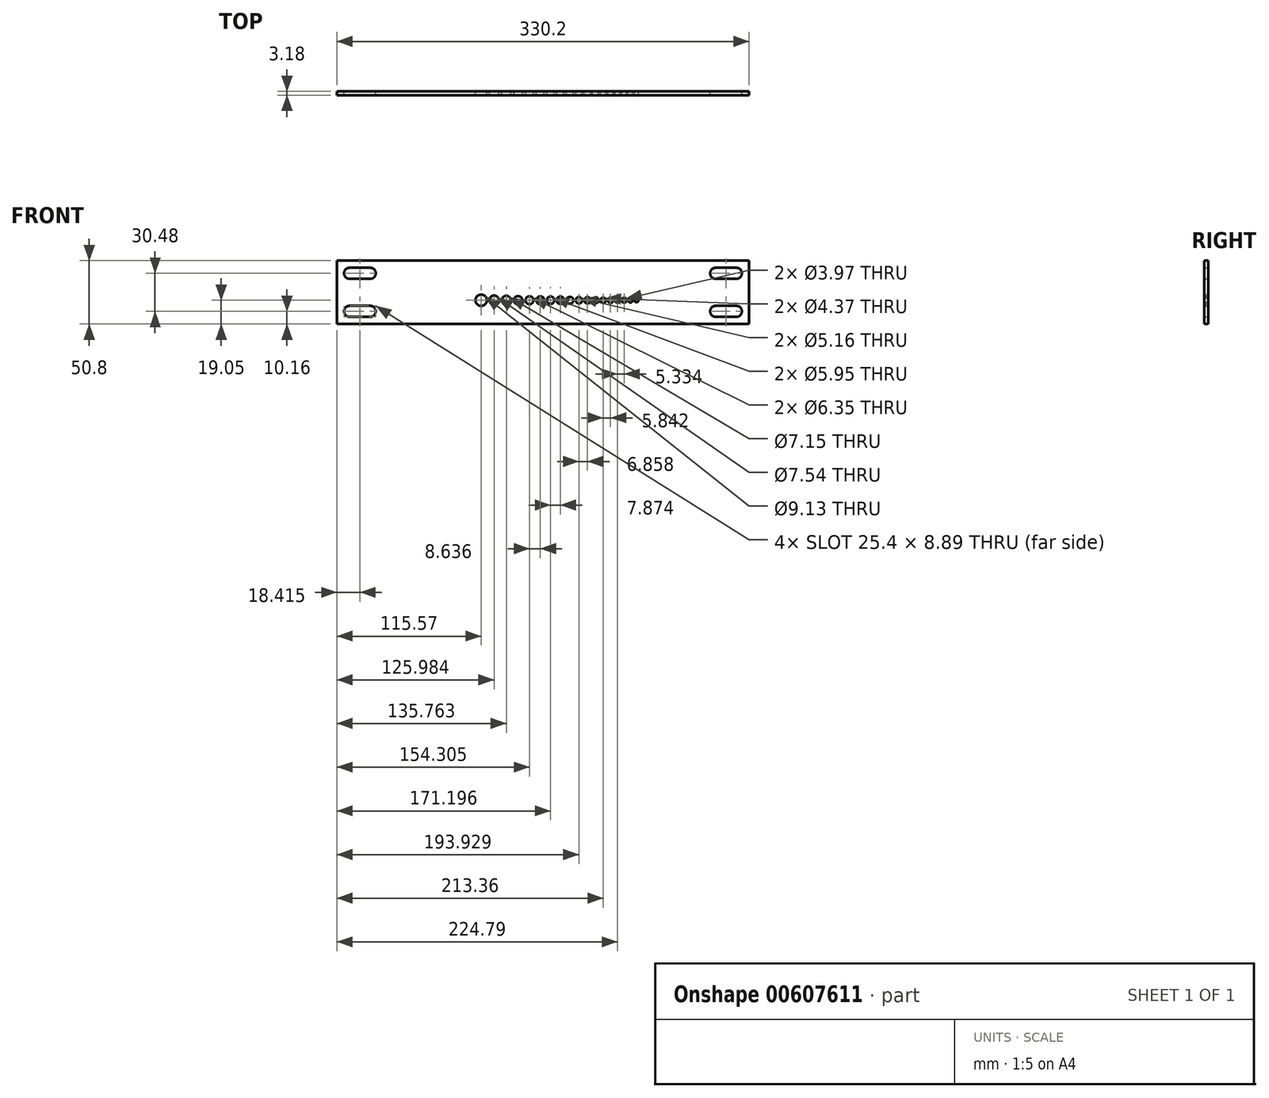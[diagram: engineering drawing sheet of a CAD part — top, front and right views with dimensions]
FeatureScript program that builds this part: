
annotation { "Feature Type Name" : "Feature", "Feature Type Description" : "" }
export const myFeature = defineFeature(function(context is Context, id is Id, definition is map)
    precondition{}
    {
        {
            var Q0;
            Q0=qCreatedBy(makeId("Front.planeOp"),FACE);
            var sketch = newSketch(context, id + "F0", { "sketchPlane" : qUnion([Q0])});
            skLineSegment(sketch, "E0.bottom", {"start": v(165.1, 25.4) * mm, "end": v(-165.1, 25.4) * mm});
            skLineSegment(sketch, "E0.top", {"start": v(165.1, -25.4) * mm, "end": v(-165.1, -25.4) * mm});
            skLineSegment(sketch, "E0.left", {"start": v(165.1, 25.4) * mm, "end": v(165.1, -25.4) * mm});
            skLineSegment(sketch, "E0.right", {"start": v(-165.1, 25.4) * mm, "end": v(-165.1, -25.4) * mm});
            skPoint(sketch, "E0.middle", {"position": v(0, 0) * mm});
            skLineSegment(sketch, "E1", {"start": v(-165.1, -6.35) * mm, "end": v(165.1, -6.35) * mm});
            skLineSegment(sketch, "E2.bottom", {"start": v(-138.43, 19.68) * mm, "end": v(-154.94, 19.68) * mm});
            skLineSegment(sketch, "E2.top", {"start": v(-138.43, 10.8) * mm, "end": v(-154.94, 10.8) * mm});
            skLineSegment(sketch, "E2.left", {"start": v(-138.43, 19.68) * mm, "end": v(-138.43, 10.8) * mm});
            skLineSegment(sketch, "E2.right", {"start": v(-154.94, 19.68) * mm, "end": v(-154.94, 10.8) * mm});
            skArc(sketch, "E3", {"start": v(-138.43, 10.8) * mm, "mid": v(-133.99, 15.24) * mm, "end": v(-138.43, 19.68) * mm});
            skArc(sketch, "E4", {"start": v(-154.94, 19.68) * mm, "mid": v(-159.39, 15.24) * mm, "end": v(-154.94, 10.8) * mm});
            skLineSegment(sketch, "E5.bottom", {"start": v(154.94, 19.69) * mm, "end": v(138.43, 19.69) * mm});
            skLineSegment(sketch, "E5.top", {"start": v(154.94, 10.8) * mm, "end": v(138.43, 10.8) * mm});
            skLineSegment(sketch, "E5.left", {"start": v(154.94, 19.69) * mm, "end": v(154.94, 10.8) * mm});
            skLineSegment(sketch, "E5.right", {"start": v(138.43, 19.69) * mm, "end": v(138.43, 10.8) * mm});
            skArc(sketch, "E6", {"start": v(154.94, 10.8) * mm, "mid": v(159.39, 15.24) * mm, "end": v(154.94, 19.69) * mm});
            skArc(sketch, "E7", {"start": v(138.43, 19.69) * mm, "mid": v(133.99, 15.24) * mm, "end": v(138.43, 10.8) * mm});
            skLineSegment(sketch, "E8.bottom", {"start": v(154.94, -10.8) * mm, "end": v(138.43, -10.8) * mm});
            skLineSegment(sketch, "E8.top", {"start": v(154.94, -19.68) * mm, "end": v(138.43, -19.68) * mm});
            skLineSegment(sketch, "E8.left", {"start": v(154.94, -10.8) * mm, "end": v(154.94, -19.68) * mm});
            skLineSegment(sketch, "E8.right", {"start": v(138.43, -10.8) * mm, "end": v(138.43, -19.68) * mm});
            skArc(sketch, "E9", {"start": v(154.94, -19.68) * mm, "mid": v(159.39, -15.24) * mm, "end": v(154.94, -10.8) * mm});
            skArc(sketch, "E10", {"start": v(138.43, -10.8) * mm, "mid": v(133.99, -15.24) * mm, "end": v(138.43, -19.68) * mm});
            skLineSegment(sketch, "E11.bottom", {"start": v(-138.43, -10.8) * mm, "end": v(-154.94, -10.8) * mm});
            skLineSegment(sketch, "E11.top", {"start": v(-138.43, -19.69) * mm, "end": v(-154.94, -19.69) * mm});
            skLineSegment(sketch, "E11.left", {"start": v(-138.43, -10.8) * mm, "end": v(-138.43, -19.69) * mm});
            skLineSegment(sketch, "E11.right", {"start": v(-154.94, -10.8) * mm, "end": v(-154.94, -19.69) * mm});
            skArc(sketch, "E12", {"start": v(-138.43, -19.69) * mm, "mid": v(-133.99, -15.24) * mm, "end": v(-138.43, -10.8) * mm});
            skArc(sketch, "E13", {"start": v(-154.94, -10.8) * mm, "mid": v(-159.39, -15.24) * mm, "end": v(-154.94, -19.69) * mm});
            skCircle(sketch, "E14", {"center": v(-49.53, -6.35) * mm, "radius": 4.56 * mm});
            skCircle(sketch, "E15", {"center": v(-39.12, -6.35) * mm, "radius": 3.77 * mm});
            skCircle(sketch, "E16", {"center": v(-29.34, -6.35) * mm, "radius": 3.57 * mm});
            skCircle(sketch, "E17", {"center": v(-19.94, -6.35) * mm, "radius": 3.37 * mm});
            skCircle(sketch, "E18", {"center": v(-10.8, -6.35) * mm, "radius": 3.18 * mm});
            skCircle(sketch, "E19", {"center": v(-2.16, -6.35) * mm, "radius": 3.18 * mm});
            skCircle(sketch, "E20", {"center": v(6.1, -6.35) * mm, "radius": 2.98 * mm});
            skCircle(sketch, "E21", {"center": v(13.97, -6.35) * mm, "radius": 2.98 * mm});
            skCircle(sketch, "E22", {"center": v(21.6, -6.35) * mm, "radius": 2.78 * mm});
            skCircle(sketch, "E23", {"center": v(28.83, -6.35) * mm, "radius": 2.58 * mm});
            skCircle(sketch, "E24", {"center": v(35.69, -6.35) * mm, "radius": 2.58 * mm});
            skCircle(sketch, "E25", {"center": v(42.16, -6.35) * mm, "radius": 2.38 * mm});
            skCircle(sketch, "E26", {"center": v(48.26, -6.35) * mm, "radius": 2.18 * mm});
            skCircle(sketch, "E27", {"center": v(54.1, -6.35) * mm, "radius": 2.18 * mm});
            skCircle(sketch, "E28", {"center": v(59.7, -6.35) * mm, "radius": 1.99 * mm});
            skCircle(sketch, "E29", {"center": v(65.02, -6.35) * mm, "radius": 1.99 * mm});
            skCircle(sketch, "E30", {"center": v(70.1, -6.35) * mm, "radius": 1.79 * mm});
            skCircle(sketch, "E31", {"center": v(74.93, -6.35) * mm, "radius": 1.59 * mm});
            skSolve(sketch);
        }
        {
            var Q0;
            Q0 = qSketchRegion(id + "F0", true);
            extrude(context, id + "F1", {"entities" : qUnion([Q0]), "depth" : 3.17 * mm, "offsetDistance" : 25.4 * mm});
        }
        {
            var Q0;
            Q0=makeQuery(id+"F1.opExtrude","CAP_EDGE",EDGE,{"disambiguationData":[OSD([sQuery(id+"F0.wireOp",EDGE,"E14")])],"isStart":false});
            var Q1;
            Q1=makeQuery(id+"F1.opExtrude","CAP_EDGE",EDGE,{"disambiguationData":[OSD([sQuery(id+"F0.wireOp",EDGE,"E15")])],"isStart":false});
            var Q2;
            Q2=makeQuery(id+"F1.opExtrude","CAP_EDGE",EDGE,{"disambiguationData":[OSD([sQuery(id+"F0.wireOp",EDGE,"E16")])],"isStart":false});
            var Q3;
            Q3=makeQuery(id+"F1.opExtrude","CAP_EDGE",EDGE,{"disambiguationData":[OSD([sQuery(id+"F0.wireOp",EDGE,"E17")])],"isStart":false});
            var Q4;
            Q4=makeQuery(id+"F1.opExtrude","CAP_EDGE",EDGE,{"disambiguationData":[OSD([sQuery(id+"F0.wireOp",EDGE,"E18")])],"isStart":false});
            var Q5;
            Q5=makeQuery(id+"F1.opExtrude","CAP_EDGE",EDGE,{"disambiguationData":[OSD([sQuery(id+"F0.wireOp",EDGE,"E19")])],"isStart":false});
            var Q6;
            Q6=makeQuery(id+"F1.opExtrude","CAP_EDGE",EDGE,{"disambiguationData":[OSD([sQuery(id+"F0.wireOp",EDGE,"E20")])],"isStart":false});
            var Q7;
            Q7=makeQuery(id+"F1.opExtrude","CAP_EDGE",EDGE,{"disambiguationData":[OSD([sQuery(id+"F0.wireOp",EDGE,"E21")])],"isStart":false});
            var Q8;
            Q8=makeQuery(id+"F1.opExtrude","CAP_EDGE",EDGE,{"disambiguationData":[OSD([sQuery(id+"F0.wireOp",EDGE,"E22")])],"isStart":false});
            var Q9;
            Q9=makeQuery(id+"F1.opExtrude","CAP_EDGE",EDGE,{"disambiguationData":[OSD([sQuery(id+"F0.wireOp",EDGE,"E23")])],"isStart":false});
            var Q10;
            Q10=makeQuery(id+"F1.opExtrude","CAP_EDGE",EDGE,{"disambiguationData":[OSD([sQuery(id+"F0.wireOp",EDGE,"E24")])],"isStart":false});
            var Q11;
            Q11=makeQuery(id+"F1.opExtrude","CAP_EDGE",EDGE,{"disambiguationData":[OSD([sQuery(id+"F0.wireOp",EDGE,"E25")])],"isStart":false});
            var Q12;
            Q12=makeQuery(id+"F1.opExtrude","CAP_EDGE",EDGE,{"disambiguationData":[OSD([sQuery(id+"F0.wireOp",EDGE,"E26")])],"isStart":false});
            var Q13;
            Q13=makeQuery(id+"F1.opExtrude","CAP_EDGE",EDGE,{"disambiguationData":[OSD([sQuery(id+"F0.wireOp",EDGE,"E27")])],"isStart":false});
            var Q14;
            Q14=makeQuery(id+"F1.opExtrude","CAP_EDGE",EDGE,{"disambiguationData":[OSD([sQuery(id+"F0.wireOp",EDGE,"E28")])],"isStart":false});
            var Q15;
            Q15=makeQuery(id+"F1.opExtrude","CAP_EDGE",EDGE,{"disambiguationData":[OSD([sQuery(id+"F0.wireOp",EDGE,"E29")])],"isStart":false});
            var Q16;
            Q16=makeQuery(id+"F1.opExtrude","CAP_EDGE",EDGE,{"disambiguationData":[OSD([sQuery(id+"F0.wireOp",EDGE,"E30")])],"isStart":false});
            var Q17;
            Q17=makeQuery(id+"F1.opExtrude","CAP_EDGE",EDGE,{"disambiguationData":[OSD([sQuery(id+"F0.wireOp",EDGE,"E31")])],"isStart":false});
            var Q18;
            Q18=makeQuery(id+"F1.opExtrude","CAP_EDGE",EDGE,{"disambiguationData":[OSD([sQuery(id+"F0.wireOp",EDGE,"E14")])],"isStart":true});
            var Q19;
            Q19=makeQuery(id+"F1.opExtrude","CAP_EDGE",EDGE,{"disambiguationData":[OSD([sQuery(id+"F0.wireOp",EDGE,"E15")])],"isStart":true});
            var Q20;
            Q20=makeQuery(id+"F1.opExtrude","CAP_EDGE",EDGE,{"disambiguationData":[OSD([sQuery(id+"F0.wireOp",EDGE,"E16")])],"isStart":true});
            var Q21;
            Q21=makeQuery(id+"F1.opExtrude","CAP_EDGE",EDGE,{"disambiguationData":[OSD([sQuery(id+"F0.wireOp",EDGE,"E17")])],"isStart":true});
            var Q22;
            Q22=makeQuery(id+"F1.opExtrude","CAP_EDGE",EDGE,{"disambiguationData":[OSD([sQuery(id+"F0.wireOp",EDGE,"E18")])],"isStart":true});
            var Q23;
            Q23=makeQuery(id+"F1.opExtrude","CAP_EDGE",EDGE,{"disambiguationData":[OSD([sQuery(id+"F0.wireOp",EDGE,"E19")])],"isStart":true});
            var Q24;
            Q24=makeQuery(id+"F1.opExtrude","CAP_EDGE",EDGE,{"disambiguationData":[OSD([sQuery(id+"F0.wireOp",EDGE,"E20")])],"isStart":true});
            var Q25;
            Q25=makeQuery(id+"F1.opExtrude","CAP_EDGE",EDGE,{"disambiguationData":[OSD([sQuery(id+"F0.wireOp",EDGE,"E21")])],"isStart":true});
            var Q26;
            Q26=makeQuery(id+"F1.opExtrude","CAP_EDGE",EDGE,{"disambiguationData":[OSD([sQuery(id+"F0.wireOp",EDGE,"E22")])],"isStart":true});
            var Q27;
            Q27=makeQuery(id+"F1.opExtrude","CAP_EDGE",EDGE,{"disambiguationData":[OSD([sQuery(id+"F0.wireOp",EDGE,"E23")])],"isStart":true});
            var Q28;
            Q28=makeQuery(id+"F1.opExtrude","CAP_EDGE",EDGE,{"disambiguationData":[OSD([sQuery(id+"F0.wireOp",EDGE,"E24")])],"isStart":true});
            var Q29;
            Q29=makeQuery(id+"F1.opExtrude","CAP_EDGE",EDGE,{"disambiguationData":[OSD([sQuery(id+"F0.wireOp",EDGE,"E25")])],"isStart":true});
            var Q30;
            Q30=makeQuery(id+"F1.opExtrude","CAP_EDGE",EDGE,{"disambiguationData":[OSD([sQuery(id+"F0.wireOp",EDGE,"E26")])],"isStart":true});
            var Q31;
            Q31=makeQuery(id+"F1.opExtrude","CAP_EDGE",EDGE,{"disambiguationData":[OSD([sQuery(id+"F0.wireOp",EDGE,"E27")])],"isStart":true});
            var Q32;
            Q32=makeQuery(id+"F1.opExtrude","CAP_EDGE",EDGE,{"disambiguationData":[OSD([sQuery(id+"F0.wireOp",EDGE,"E28")])],"isStart":true});
            var Q33;
            Q33=makeQuery(id+"F1.opExtrude","CAP_EDGE",EDGE,{"disambiguationData":[OSD([sQuery(id+"F0.wireOp",EDGE,"E29")])],"isStart":true});
            var Q34;
            Q34=makeQuery(id+"F1.opExtrude","CAP_EDGE",EDGE,{"disambiguationData":[OSD([sQuery(id+"F0.wireOp",EDGE,"E30")])],"isStart":true});
            var Q35;
            Q35=makeQuery(id+"F1.opExtrude","CAP_EDGE",EDGE,{"disambiguationData":[OSD([sQuery(id+"F0.wireOp",EDGE,"E31")])],"isStart":true});
            fillet(context, id + "F2", {"entities" : qUnion([Q0, Q1, Q2, Q3, Q4, Q5, Q6, Q7, Q8, Q9, Q10, Q11, Q12, Q13, Q14, Q15, Q16, Q17, Q18, Q19, Q20, Q21, Q22, Q23, Q24, Q25, Q26, Q27, Q28, Q29, Q30, Q31, Q32, Q33, Q34, Q35]), "radius" : 0.5 * mm, "tangentPropagation" : true, "allowEdgeOverflow" : false});
        }
    });
